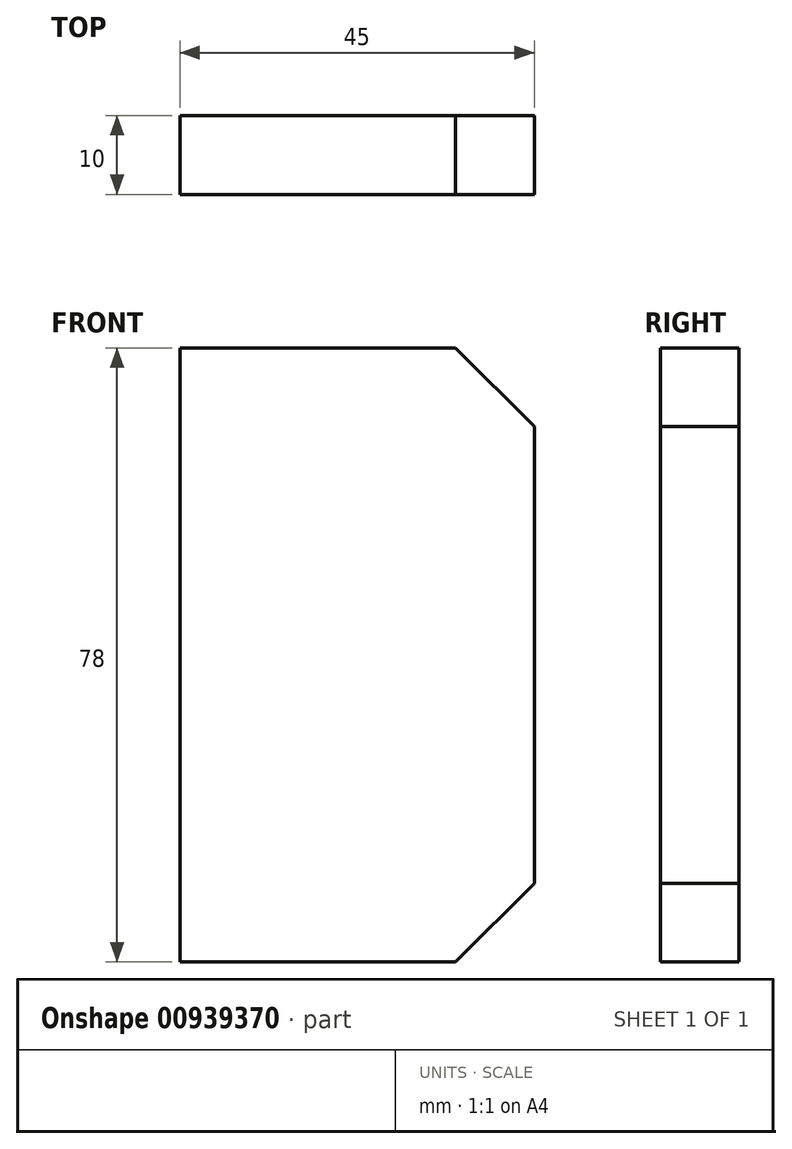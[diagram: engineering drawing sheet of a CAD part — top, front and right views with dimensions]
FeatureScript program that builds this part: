
annotation { "Feature Type Name" : "Feature", "Feature Type Description" : "" }
export const myFeature = defineFeature(function(context is Context, id is Id, definition is map)
    precondition{}
    {
        {
            var Q0;
            Q0=qCreatedBy(makeId("Front.planeOp"),FACE);
            var sketch = newSketch(context, id + "F0", { "sketchPlane" : qUnion([Q0])});
            skLineSegment(sketch, "E0.bottom", {"start": v(22.5, 39) * mm, "end": v(-22.5, 39) * mm});
            skLineSegment(sketch, "E0.top", {"start": v(22.5, -39) * mm, "end": v(-22.5, -39) * mm});
            skLineSegment(sketch, "E0.left", {"start": v(22.5, 39) * mm, "end": v(22.5, -39) * mm});
            skLineSegment(sketch, "E0.right", {"start": v(-22.5, 39) * mm, "end": v(-22.5, -39) * mm});
            skPoint(sketch, "E0.middle", {"position": v(0, 0) * mm});
            skSolve(sketch);
        }
        {
            var Q0;
            Q0=makeQuery(id+"F0.imprint","IMPRINT",FACE,{"disambiguationData":[TD([[makeQuery(id+"F0.imprint","IMPRINT",EDGE,{"derivedFrom":sQuery(id+"F0.wireOp",EDGE,"E0.bottom")}),1.0]])]});
            extrude(context, id + "F1", {"entities" : qUnion([Q0]), "depth" : 10 * mm, "offsetDistance" : 25 * mm});
        }
        {
            var Q0;
            Q0=makeQuery(id+"F1.opExtrude","SWEPT_EDGE",EDGE,{"disambiguationData":[OSD([sQuery(id+"F0.wireOp",EDGE,"E0.bottom"),sQuery(id+"F0.wireOp",EDGE,"E0.left")])]});
            var Q1;
            Q1=makeQuery(id+"F1.opExtrude","SWEPT_EDGE",EDGE,{"disambiguationData":[OSD([sQuery(id+"F0.wireOp",EDGE,"E0.top"),sQuery(id+"F0.wireOp",EDGE,"E0.left")])]});
            chamfer(context, id + "F2", {"entities" : qUnion([Q0, Q1]), "width" : 10 * mm, "tangentPropagation" : true});
        }
    });
